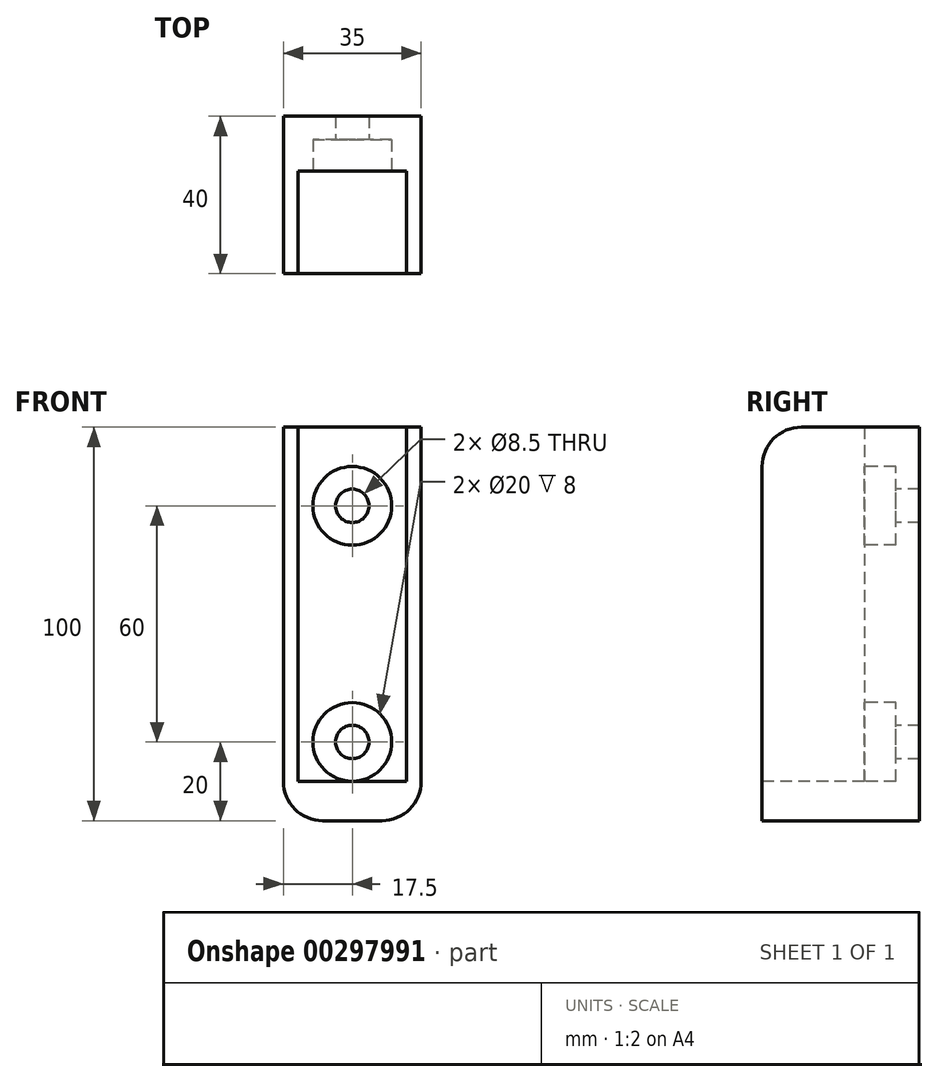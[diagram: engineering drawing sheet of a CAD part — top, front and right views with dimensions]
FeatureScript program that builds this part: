
annotation { "Feature Type Name" : "Feature", "Feature Type Description" : "" }
export const myFeature = defineFeature(function(context is Context, id is Id, definition is map)
    precondition{}
    {
        {
            var Q0;
            Q0=qCreatedBy(makeId("Front.planeOp"),FACE);
            var sketch = newSketch(context, id + "F0", { "sketchPlane" : qUnion([Q0])});
            skLineSegment(sketch, "E0.bottom", {"start": v(-17.5, 50) * mm, "end": v(17.5, 50) * mm});
            skLineSegment(sketch, "E0.top", {"start": v(-17.5, -50) * mm, "end": v(17.5, -50) * mm});
            skLineSegment(sketch, "E0.left", {"start": v(-17.5, 50) * mm, "end": v(-17.5, -50) * mm});
            skLineSegment(sketch, "E0.right", {"start": v(17.5, 50) * mm, "end": v(17.5, -50) * mm});
            skPoint(sketch, "E0.middle", {"position": v(0, 0) * mm});
            skSolve(sketch);
        }
        {
            var Q0;
            Q0 = qSketchRegion(id + "F0", true);
            extrude(context, id + "F1", {"entities" : qUnion([Q0]), "depth" : 40 * mm});
        }
        {
            var Q0;
            Q0=makeQuery(id+"F1.opExtrude","CAP_FACE",FACE,{"disambiguationData":[OSD([sQuery(id+"F0.wireOp",EDGE,"E0.bottom"),sQuery(id+"F0.wireOp",EDGE,"E0.top"),sQuery(id+"F0.wireOp",EDGE,"E0.left"),sQuery(id+"F0.wireOp",EDGE,"E0.right")])],"isStart":false});
            var sketch = newSketch(context, id + "F2", { "sketchPlane" : qUnion([Q0])});
            skLineSegment(sketch, "E1", {"start": v(-13.75, 50) * mm, "end": v(-13.75, -40) * mm});
            skLineSegment(sketch, "E2", {"start": v(-13.75, -40) * mm, "end": v(13.75, -40) * mm});
            skLineSegment(sketch, "E3", {"start": v(13.75, -40) * mm, "end": v(13.75, 50) * mm});
            skLineSegment(sketch, "E4", {"start": v(-13.75, 50) * mm, "end": v(13.75, 50) * mm});
            skSolve(sketch);
        }
        {
            var Q0;
            Q0 = qSketchRegion(id + "F2", true);
            extrude(context, id + "F3", {"entities" : qUnion([Q0]), "operationType" : NewBodyOperationType.REMOVE, "oppositeDirection" : true, "depth" : 26 * mm});
        }
        {
            var Q0;
            {var subQ0=sQuery(id+"F0.wireOp",EDGE,"E0.bottom");var subQ1=sQuery(id+"F0.wireOp",EDGE,"E0.left");Q0=makeQuery(id+"F3.boolean.opBoolean","SPLIT",EDGE,{"disambiguationData":[TD([makeQuery(id+"F1.opExtrude","SWEPT_FACE",FACE,{"disambiguationData":[OSD([subQ1])]})])],"derivedFrom":makeQuery(id+"F1.opExtrude","CAP_EDGE",EDGE,{"disambiguationData":[OSD([subQ0])],"isStart":false})});}
            var Q1;
            {var subQ0=sQuery(id+"F0.wireOp",EDGE,"E0.bottom");var subQ1=sQuery(id+"F0.wireOp",EDGE,"E0.right");Q1=makeQuery(id+"F3.boolean.opBoolean","SPLIT",EDGE,{"disambiguationData":[TD([makeQuery(id+"F1.opExtrude","SWEPT_FACE",FACE,{"disambiguationData":[OSD([subQ1])]})])],"derivedFrom":makeQuery(id+"F1.opExtrude","CAP_EDGE",EDGE,{"disambiguationData":[OSD([subQ0])],"isStart":false})});}
            var Q2;
            Q2=makeQuery(id+"F1.opExtrude","SWEPT_EDGE",EDGE,{"disambiguationData":[OSD([sQuery(id+"F0.wireOp",EDGE,"E0.top"),sQuery(id+"F0.wireOp",EDGE,"E0.left")])]});
            var Q3;
            Q3=makeQuery(id+"F1.opExtrude","SWEPT_EDGE",EDGE,{"disambiguationData":[OSD([sQuery(id+"F0.wireOp",EDGE,"E0.top"),sQuery(id+"F0.wireOp",EDGE,"E0.right")])]});
            fillet(context, id + "F4", {"entities" : qUnion([Q0, Q1, Q2, Q3]), "radius" : 10 * mm, "tangentPropagation" : true, "allowEdgeOverflow" : false});
        }
        {
            var Q0;
            Q0=makeQuery(id+"F3.boolean.opBoolean","COPY",FACE,{"derivedFrom":makeQuery(id+"F3.opExtrude","CAP_FACE",FACE,{"disambiguationData":[OSD([sQuery(id+"F2.wireOp",EDGE,"E1"),sQuery(id+"F2.wireOp",EDGE,"E2"),sQuery(id+"F2.wireOp",EDGE,"E3"),sQuery(id+"F2.wireOp",EDGE,"E4")])],"isStart":false})});
            var sketch = newSketch(context, id + "F5", { "sketchPlane" : qUnion([Q0])});
            skPoint(sketch, "E5", {"position": v(0, 30) * mm});
            skPoint(sketch, "E6", {"position": v(0, -30) * mm});
            skSolve(sketch);
        }
        {
            var Q0;
            Q0=sQuery(id+"F5.wireOp",VERTEX,"E5");
            var Q1;
            Q1=sQuery(id+"F5.wireOp",VERTEX,"E6");
            var Q2;
            Q2=makeQuery(id+"F1.opExtrude","SWEPT_BODY",BODY,{"disambiguationData":[OSD([sQuery(id+"F0.wireOp",EDGE,"E0.bottom"),sQuery(id+"F0.wireOp",EDGE,"E0.top"),sQuery(id+"F0.wireOp",EDGE,"E0.left"),sQuery(id+"F0.wireOp",EDGE,"E0.right")])]});
            hole(context, id + "F6", {"style" : HoleStyle.C_BORE, "endStyle" : HoleEndStyle.THROUGH, "holeDiameter" : 8.5 * mm, "cBoreDiameter" : 20 * mm, "cBoreDepth" : 8 * mm, "tappedDepth" : 12 * mm, "tapClearance" : 3, "locations" : qUnion([Q0, Q1]), "scope" : qUnion([Q2])});
        }
    });
